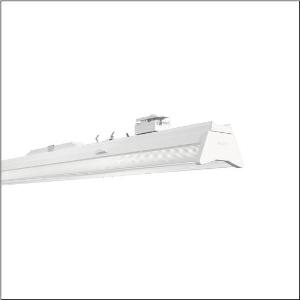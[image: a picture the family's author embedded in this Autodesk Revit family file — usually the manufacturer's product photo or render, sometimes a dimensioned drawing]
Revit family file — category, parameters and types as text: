
# Revit family: licross_r__21_performance_mo_52tm167n445g_e37c
name_source: partatom
category: Lighting Fixtures
units: mm (PartAtom-declared; Revit-internal decimal feet)

## family parameters
Cut with Voids When Loaded = No
Host = Face
Light Source = No
Part Type = Normal
Room Calculation Point = No
Round Connector Dimension = Use Diameter
Shared = No

## types (1)
- Licross® 21 Performance MO (1 x LED, 4580 lm, 24.7 W, 4000K)
    Apparent Load = 25 VA
    CIE Flux Codes = 66 88 96 79 100
    Color Rendering = 80
    Color Temperature = 4000K
    Default Elevation = 1800 mm
    Description = Licross® 21 Performance MO, luminaire insert, of sheet steel, galvanised, coil coated, white, length: 1.500mm, width: 120mm, height: 123mm, LED rated luminous flux: 4.580lm, light colour: 840, control gear: ON/OFF, with plug, 3-pole, with phase selection, mains connection: 220..240V, AC, 50/60Hz, rated input power: 25W, halogen-free wiring, primary light control with lens, of plastic, primary optical cover: cover, of PMMA, CAT 2 (L<= 3000cd/m²), light emission: direct/indirect distribution, primary light characteristic: symmetric, protection rating (complete): IP40, insulation class (complete): insulation class I (protective earthing), certification: CE, ENEC, UKCA, protection symbol: D if used in an environment without relevant dust loads with corresponding accessories, impact resistance: IK06, permissible ambient temperature for indoor applications: -35..+55°C, corresponds to IFS (International Featured Standards) requirements for safety and quality in the food industry, reducing of maximum allowable ambient temperature of 5°C with ceiling mounting, LABS conformity tested according to VDMA 24364:2018-05, packaging unit: 1 piece
    Height = 114 mm
    Lamp = 1 x LED
    Lamp Light Flux = 4580 lm
    Lamp Power = 24.7 W
    Lamp count = 1
    Length = 1500 mm
    Luminous efficacy = 185 lm/W
    Manufacturer = Siteco
    ModVariant = No
    Model = 52TM167N445G
    Mounting Place = Ceiling
    Mounting Type = Pendant
    Number of Poles = 1
    OnlyDefault = Yes
    Power Factor = 1
    Product Name = Licross® 21 Performance MO
    Product group = luminaire insert
    ProductGroupID = 901
    Protection Class = Protection class I
    Protection Degree = IP 40
    RLX_Detail_Level = 1
    RLX_Emergency_Light_Flux = 0 lm
    RLX_Emergency_Type = 0
    RLX_Emergency_Type_DB = No
    RlxData = <blob elided: 30409 chars, md5=89b325fc>
    Socket = socket
    Standby Power = 0 W
    System Light Flux = 4580 lm
    System Power = 25 W
    Type Comments = Product without accessories
    Type Image = l_1256138.jpg
    URL = http://relux.com
    VarID = ---
    Voltage = 0 V
    Weight = 0.00 kg
    Width = 120 mm

## geometry (parser evidence)
native form markers: Blend x4, Sweep x12
no freeform markers — native parametric forms only
